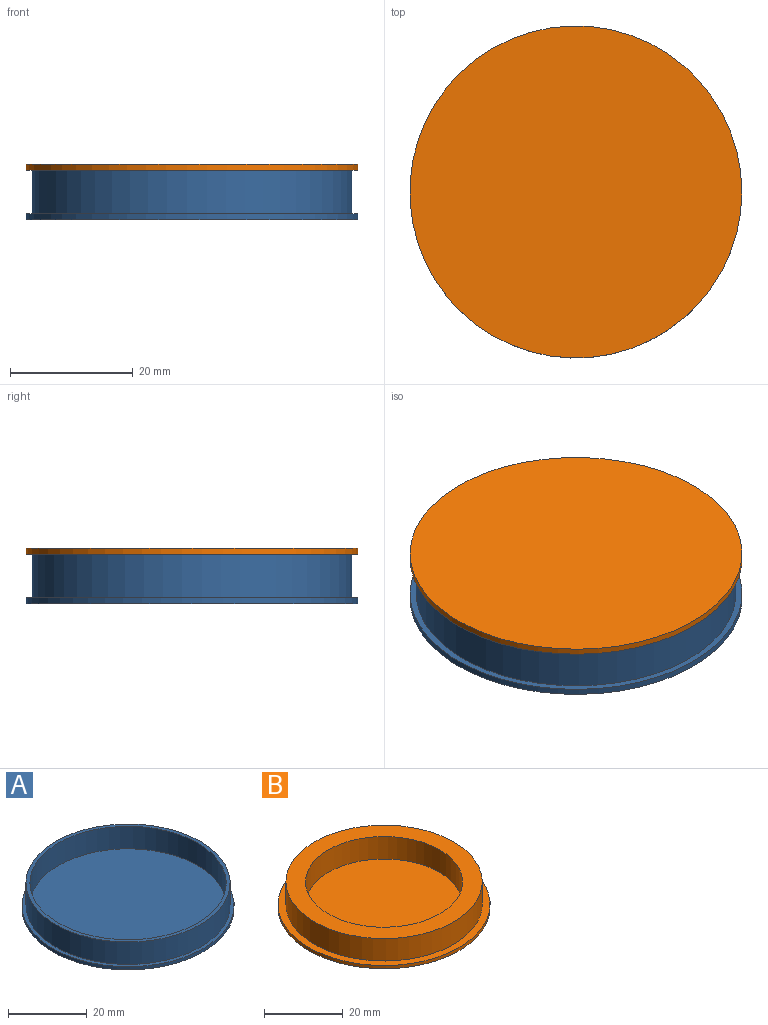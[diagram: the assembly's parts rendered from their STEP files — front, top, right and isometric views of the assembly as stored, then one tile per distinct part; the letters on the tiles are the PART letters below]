
ASSEMBLY  parts=2 mates=1
PART A: 7 faces, bbox 54x54x8 mm
  f0: cylinder r=27mm len=54mm, axis (0,0,-1), area 169.6mm2, adj f1,f2
  f1: plane 54x54mm, normal (0,0,1), area 166.5mm2, adj f0,f4
  f2: plane 54x54mm, normal (0,0,-1), area 2290.2mm2, adj f0
  f3: cylinder r=25mm len=50mm, axis (0,0,-1), area 1099.6mm2, adj f5,f6
  f4: cylinder r=26mm len=52mm, axis (0,0,-1), area 1143.5mm2, adj f1,f5
  f5: plane 52x52mm, normal (0,0,1), area 160.2mm2, adj f3,f4
  f6: plane 50x50mm, normal (0,0,1), area 1963.5mm2, adj f3
PART B: 7 faces, bbox 54x54x8 mm
  f0: cylinder r=27mm len=54mm, axis (0,0,-1), area 169.6mm2, adj f1,f2
  f1: plane 54x54mm, normal (0,0,1), area 326.7mm2, adj f0,f3
  f2: plane 54x54mm, normal (0,0,-1), area 2290.2mm2, adj f0
  f3: cylinder r=25mm len=50mm, axis (0,0,-1), area 1099.6mm2, adj f1,f4
  f4: plane 50x50mm, normal (0,0,1), area 706.9mm2, adj f3,f5
  f5: cylinder r=20mm len=40mm, axis (0,0,1), area 879.6mm2, adj f4,f6
  f6: plane 40x40mm, normal (0,0,1), area 1256.6mm2, adj f5
PLACE A at identity
PLACE B rot(axis=(1,0,0),180deg) t=(0,0,9)mm
MATE fastened B.f0 <-> A.f0  axis (0,0,-1) through (0,0,1)mm
